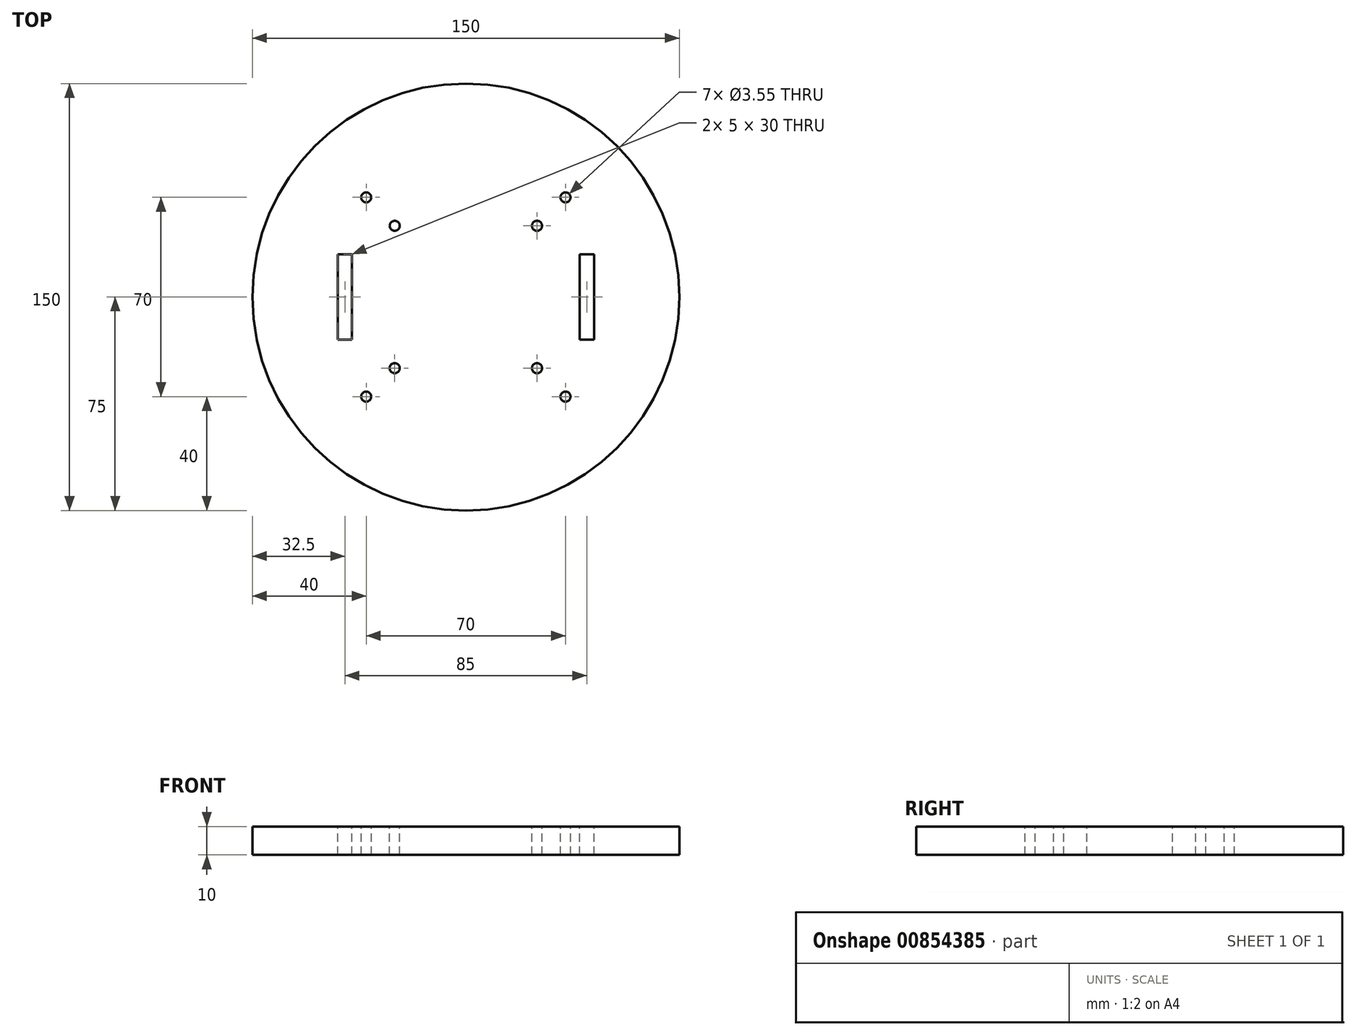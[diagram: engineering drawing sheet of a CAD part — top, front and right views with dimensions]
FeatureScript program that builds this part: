
annotation { "Feature Type Name" : "Feature", "Feature Type Description" : "" }
export const myFeature = defineFeature(function(context is Context, id is Id, definition is map)
    precondition{}
    {
        {
            var Q0;
            Q0=qCreatedBy(makeId("Top.planeOp"),FACE);
            var sketch = newSketch(context, id + "F0", { "sketchPlane" : qUnion([Q0])});
            skCircle(sketch, "E0", {"center": v(0, 0) * mm, "radius": 75 * mm});
            skSolve(sketch);
        }
        {
            var Q0;
            Q0 = qSketchRegion(id + "F0", true);
            extrude(context, id + "F1", {"entities" : qUnion([Q0]), "depth" : 10 * mm, "offsetDistance" : 25 * mm});
        }
        {
            var Q0;
            Q0=makeQuery(id+"F1.opExtrude","CAP_FACE",FACE,{"disambiguationData":[OSD([sQuery(id+"F0.wireOp",EDGE,"E0")])],"isStart":false});
            var sketch = newSketch(context, id + "F2", { "sketchPlane" : qUnion([Q0])});
            skCircle(sketch, "E1", {"center": v(-35, 35) * mm, "radius": 1.77 * mm});
            skCircle(sketch, "E2", {"center": v(-25, 25) * mm, "radius": 1.76 * mm});
            skCircle(sketch, "E3", {"center": v(25, 25) * mm, "radius": 1.77 * mm});
            skCircle(sketch, "E4", {"center": v(35, 35) * mm, "radius": 1.77 * mm});
            skCircle(sketch, "E5", {"center": v(25, -25) * mm, "radius": 1.77 * mm});
            skCircle(sketch, "E6", {"center": v(35, -35) * mm, "radius": 1.77 * mm});
            skCircle(sketch, "E7", {"center": v(-25, -25) * mm, "radius": 1.77 * mm});
            skCircle(sketch, "E8", {"center": v(-35, -35) * mm, "radius": 1.77 * mm});
            skSolve(sketch);
        }
        {
            var Q0;
            Q0 = qSketchRegion(id + "F2", true);
            extrude(context, id + "F3", {"entities" : qUnion([Q0]), "operationType" : NewBodyOperationType.REMOVE, "oppositeDirection" : true, "depth" : 25 * mm, "offsetDistance" : 25 * mm});
        }
        {
            var Q0;
            Q0=makeQuery(id+"F1.opExtrude","CAP_FACE",FACE,{"disambiguationData":[OSD([sQuery(id+"F0.wireOp",EDGE,"E0")])],"isStart":false});
            var sketch = newSketch(context, id + "F4", { "sketchPlane" : qUnion([Q0])});
            skLineSegment(sketch, "E9.bottom", {"start": v(-45, 15) * mm, "end": v(-40, 15) * mm});
            skLineSegment(sketch, "E9.top", {"start": v(-45, -15) * mm, "end": v(-40, -15) * mm});
            skLineSegment(sketch, "E9.left", {"start": v(-45, 15) * mm, "end": v(-45, -15) * mm});
            skLineSegment(sketch, "E9.right", {"start": v(-40, 15) * mm, "end": v(-40, -15) * mm});
            skLineSegment(sketch, "E10.bottom", {"start": v(40, 15) * mm, "end": v(45, 15) * mm});
            skLineSegment(sketch, "E10.top", {"start": v(40, -15) * mm, "end": v(45, -15) * mm});
            skLineSegment(sketch, "E10.left", {"start": v(40, 15) * mm, "end": v(40, -15) * mm});
            skLineSegment(sketch, "E10.right", {"start": v(45, 15) * mm, "end": v(45, -15) * mm});
            skSolve(sketch);
        }
        {
            var Q0;
            Q0 = qSketchRegion(id + "F4", true);
            extrude(context, id + "F5", {"entities" : qUnion([Q0]), "operationType" : NewBodyOperationType.REMOVE, "oppositeDirection" : true, "depth" : 25 * mm, "offsetDistance" : 25 * mm});
        }
    });
